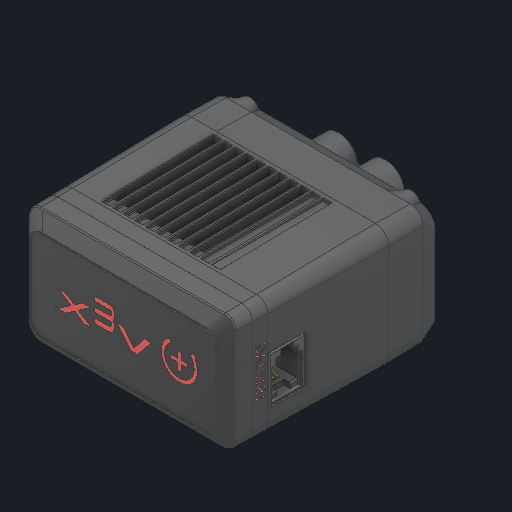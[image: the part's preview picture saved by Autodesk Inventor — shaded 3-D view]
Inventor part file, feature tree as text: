
AUTODESK INVENTOR PART (.ipt)
format: ipt  version: 2024 (Build 280153000, 153)  size: 13,054,464 bytes
history: native  units: in
note: dims shown in document units (in); Inventor stores cm internally (conversion verified against a paired STEP export)
features: other x19, sketch x2
ambient origin geometry x8: Origin, YZ Plane, XZ Plane, XY Plane, X Axis, Y Axis, Z Axis, Center Point
bodies: Solid1 (feature_tree), Solid2 (feature_tree), Solid7 (feature_tree), Solid8 (feature_tree), Solid9 (feature_tree), Solid20 (feature_tree), Solid21 (feature_tree), Solid22 (feature_tree)
feature tree (21):
  other  "V5 Motor.ipt"
  other  "Solid1::V5 Motor.ipt"
  other  "Solid2::V5 Motor.ipt"
  other  "Solid4::V5 Motor.ipt"
  other  "Solid6::V5 Motor.ipt"
  other  "Solid7::V5 Motor.ipt"
  other  "Solid8::V5 Motor.ipt"
  other  "Solid9::V5 Motor.ipt"
  other  "Solid14::V5 Motor.ipt"
  other  "Solid16::V5 Motor.ipt"
  other  "Solid17::V5 Motor.ipt"
  other  "Solid18::V5 Motor.ipt"
  other  "Solid19::V5 Motor.ipt"
  other  "Solid20::V5 Motor.ipt"
  other  "Solid21::V5 Motor.ipt"
  other  "Solid22::V5 Motor.ipt"
  other  "TaggingFeature1"
  sketch  "Sketch1"  dims[d0=0.3937in]
  sketch  "Sketch2"  dims[d4=0.0in d5=0.0in]
  other  "iInsert:1"
  other  "iInsert:2"
